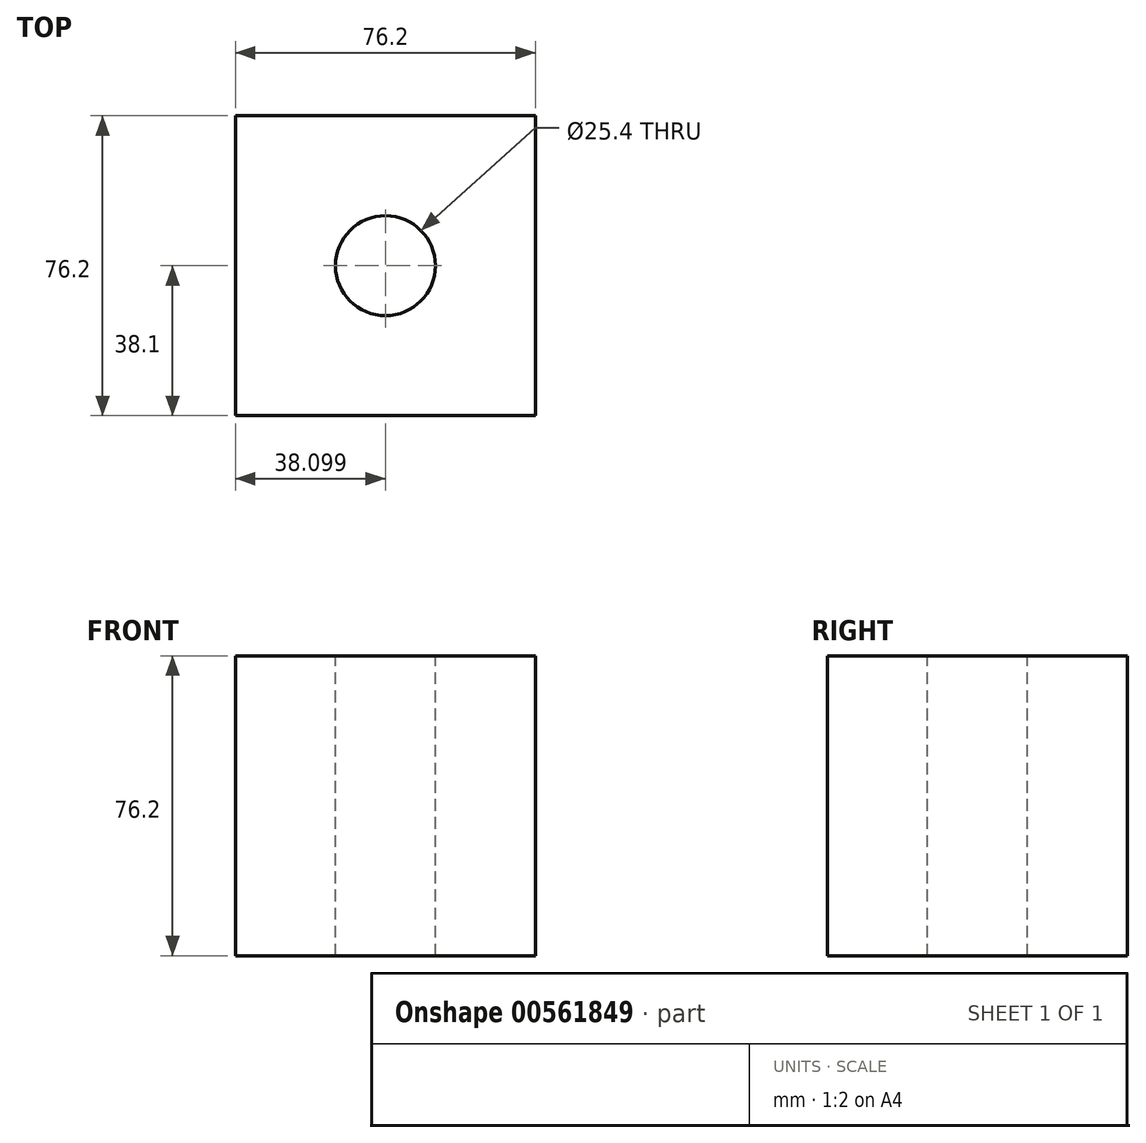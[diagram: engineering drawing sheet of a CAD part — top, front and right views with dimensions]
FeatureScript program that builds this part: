
annotation { "Feature Type Name" : "Feature", "Feature Type Description" : "" }
export const myFeature = defineFeature(function(context is Context, id is Id, definition is map)
    precondition{}
    {
        {
            var Q0;
            Q0=qCreatedBy(makeId("Front.planeOp"),FACE);
            var sketch = newSketch(context, id + "F0", { "sketchPlane" : qUnion([Q0])});
            skLineSegment(sketch, "E0.bottom", {"start": v(-32.8, -28.82) * mm, "end": v(43.4, -28.82) * mm});
            skLineSegment(sketch, "E0.top", {"start": v(-32.8, 47.38) * mm, "end": v(43.4, 47.38) * mm});
            skLineSegment(sketch, "E0.left", {"start": v(-32.8, -28.82) * mm, "end": v(-32.8, 47.38) * mm});
            skLineSegment(sketch, "E0.right", {"start": v(43.4, -28.82) * mm, "end": v(43.4, 47.38) * mm});
            skSolve(sketch);
        }
        {
            var Q0;
            Q0 = qSketchRegion(id + "F0", true);
            extrude(context, id + "F1", {"entities" : qUnion([Q0]), "depth" : 76.2 * mm, "offsetDistance" : 25.4 * mm});
        }
        {
            var Q0;
            Q0=makeQuery(id+"F1.opExtrude","SWEPT_FACE",FACE,{"disambiguationData":[OSD([sQuery(id+"F0.wireOp",EDGE,"E0.top")])]});
            var sketch = newSketch(context, id + "F2", { "sketchPlane" : qUnion([Q0])});
            skPoint(sketch, "E1", {"position": v(5.3, -38.1) * mm});
            skSolve(sketch);
        }
        {
            var Q0;
            Q0=sQuery(id+"F2.wireOp",VERTEX,"E1");
            var Q1;
            Q1=makeQuery(id+"F1.opExtrude","SWEPT_BODY",BODY,{"disambiguationData":[OSD([sQuery(id+"F0.wireOp",EDGE,"E0.bottom"),sQuery(id+"F0.wireOp",EDGE,"E0.top"),sQuery(id+"F0.wireOp",EDGE,"E0.left"),sQuery(id+"F0.wireOp",EDGE,"E0.right")])]});
            hole(context, id + "F3", {"style" : HoleStyle.SIMPLE, "endStyle" : HoleEndStyle.THROUGH, "holeDiameter" : 25.4 * mm, "isTappedThrough" : true, "tappedDepth" : 12.7 * mm, "tapClearance" : 3, "locations" : qUnion([Q0]), "scope" : qUnion([Q1])});
        }
    });
